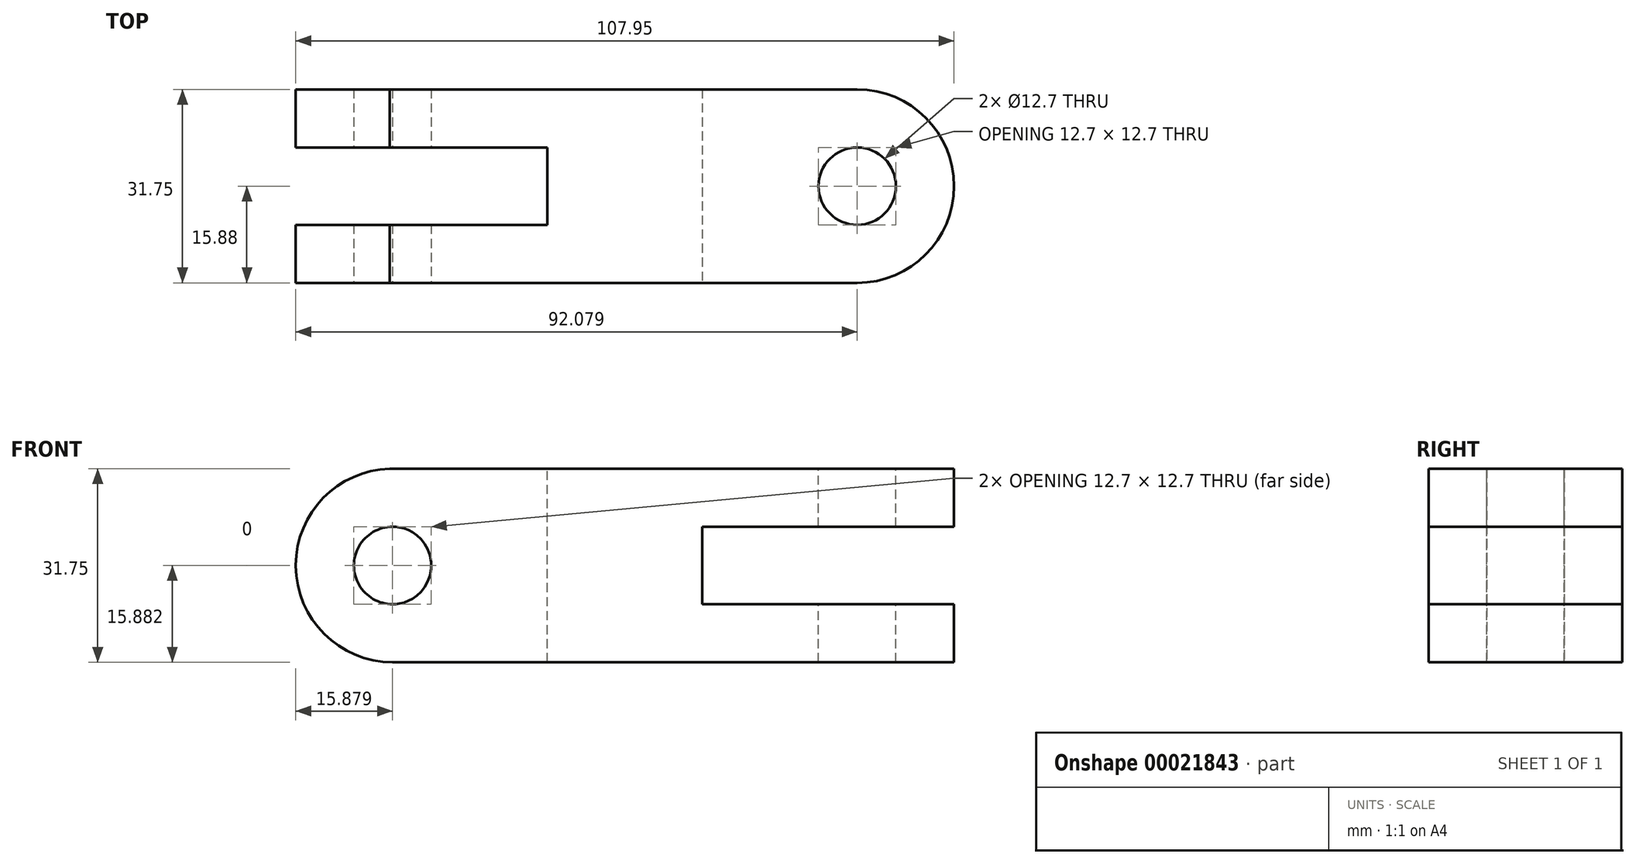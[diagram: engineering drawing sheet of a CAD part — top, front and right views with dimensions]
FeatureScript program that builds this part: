
annotation { "Feature Type Name" : "Feature", "Feature Type Description" : "" }
export const myFeature = defineFeature(function(context is Context, id is Id, definition is map)
    precondition{}
    {
        {
            var Q0;
            Q0=qCreatedBy(makeId("Top.planeOp"),FACE);
            var sketch = newSketch(context, id + "F0", { "sketchPlane" : qUnion([Q0])});
            skLineSegment(sketch, "E0.bottom", {"start": v(-44.49, 22.47) * mm, "end": v(63.46, 22.47) * mm});
            skLineSegment(sketch, "E0.top", {"start": v(-44.49, -9.28) * mm, "end": v(63.46, -9.28) * mm});
            skLineSegment(sketch, "E0.left", {"start": v(-44.49, 22.47) * mm, "end": v(-44.49, -9.28) * mm});
            skLineSegment(sketch, "E0.right", {"start": v(63.46, 22.47) * mm, "end": v(63.46, -9.28) * mm});
            skSolve(sketch);
        }
        {
            var Q0;
            Q0=makeQuery(id+"F0.imprint","IMPRINT",FACE,{"disambiguationData":[TD([[makeQuery(id+"F0.imprint","IMPRINT",EDGE,{"derivedFrom":sQuery(id+"F0.wireOp",EDGE,"E0.bottom")}),-1.0]])]});
            extrude(context, id + "F1", {"entities" : qUnion([Q0]), "depth" : 31.75 * mm});
        }
        {
            var Q0;
            Q0=makeQuery(id+"F1.opExtrude","CAP_FACE",FACE,{"disambiguationData":[OSD([sQuery(id+"F0.wireOp",EDGE,"E0.bottom"),sQuery(id+"F0.wireOp",EDGE,"E0.top"),sQuery(id+"F0.wireOp",EDGE,"E0.left"),sQuery(id+"F0.wireOp",EDGE,"E0.right")])],"isStart":false});
            var sketch = newSketch(context, id + "F2", { "sketchPlane" : qUnion([Q0])});
            skLineSegment(sketch, "E1.0", {"start": v(-44.49, 12.95) * mm, "end": v(-3.21, 12.95) * mm});
            skLineSegment(sketch, "E2.0", {"start": v(-44.49, 0.25) * mm, "end": v(-3.21, 0.25) * mm});
            skLineSegment(sketch, "E3.0", {"start": v(-3.21, 12.95) * mm, "end": v(-3.21, 0.25) * mm});
            skLineSegment(sketch, "E4.0", {"start": v(47.59, 22.47) * mm, "end": v(47.59, -9.28) * mm, "construction": true});
            skArc(sketch, "E5", {"start": v(47.59, -9.28) * mm, "mid": v(63.46, 6.6) * mm, "end": v(47.59, 22.47) * mm});
            skCircle(sketch, "E6", {"center": v(47.59, 6.6) * mm, "radius": 6.35 * mm});
            skSolve(sketch);
        }
        {
            var Q0;
            Q0=makeQuery(id+"F1.opExtrude","SWEPT_FACE",FACE,{"disambiguationData":[OSD([sQuery(id+"F0.wireOp",EDGE,"E0.top")])]});
            var sketch = newSketch(context, id + "F3", { "sketchPlane" : qUnion([Q0])});
            skLineSegment(sketch, "E7.0", {"start": v(22.19, 22.23) * mm, "end": v(63.46, 22.23) * mm});
            skLineSegment(sketch, "E8.0", {"start": v(22.19, 9.53) * mm, "end": v(63.46, 9.53) * mm});
            skLineSegment(sketch, "E9.0", {"start": v(-28.61, 31.84) * mm, "end": v(-28.61, 31.76) * mm, "construction": true});
            skLineSegment(sketch, "E10.0", {"start": v(22.19, 22.23) * mm, "end": v(22.19, 9.53) * mm});
            skLineSegment(sketch, "E11.right", {"start": v(63.46, 22.23) * mm, "end": v(63.46, 9.53) * mm});
            skLineSegment(sketch, "E12.bottom", {"start": v(41.87, 36.55) * mm, "end": v(40.98, 36.55) * mm});
            skLineSegment(sketch, "E12.top", {"start": v(41.87, 36.55) * mm, "end": v(40.98, 36.55) * mm});
            skPoint(sketch, "E13.center.orphan", {"position": v(-28.61, 15.88) * mm});
            skPoint(sketch, "E14.trimOffspring.end.orphan", {"position": v(-28.61, 0) * mm});
            skLineSegment(sketch, "E15.0", {"start": v(-28.61, 31.75) * mm, "end": v(-28.61, 0) * mm});
            skCircle(sketch, "E16", {"center": v(-28.61, 15.88) * mm, "radius": 6.35 * mm});
            skArc(sketch, "E17", {"start": v(-28.16, 31.75) * mm, "mid": v(-44.48, 16.1) * mm, "end": v(-28.61, 0) * mm});
            skLineSegment(sketch, "E18.0", {"start": v(63.46, 31.75) * mm, "end": v(63.46, 0) * mm});
            skLineSegment(sketch, "E19", {"start": v(-28.16, 31.75) * mm, "end": v(63.46, 31.75) * mm});
            skLineSegment(sketch, "E20", {"start": v(-28.61, 0) * mm, "end": v(63.46, 0) * mm});
            skSolve(sketch);
        }
        {
            var Q0;
            {var subQ2=sQuery(id+"F2.wireOp",EDGE,"E1.0");Q0=makeQuery(id+"F2.imprint","IMPRINT",FACE,{"disambiguationData":[TD([[makeQuery(id+"F2.imprint","IMPRINT",EDGE,{"derivedFrom":subQ2}),-1.0]])]});}
            var Q1;
            Q1=makeQuery(id+"F2.imprint","IMPRINT",FACE,{"disambiguationData":[TD([[makeQuery(id+"F2.imprint","IMPRINT",EDGE,{"derivedFrom":sQuery(id+"F2.wireOp",EDGE,"E6")}),1.0]])]});
            var Q2;
            {var subQ1=sQuery(id+"F2.wireOp",EDGE,"E5");var subQ3=makeQuery(id+"F1.opExtrude","CAP_EDGE",EDGE,{"disambiguationData":[OSD([sQuery(id+"F0.wireOp",EDGE,"E0.bottom")])],"isStart":false});var subQ5=makeQuery(id+"F2.imprint","INTERSECT",VERTEX,{"derivedFrom":[subQ3,subQ1]});Q2=makeQuery(id+"F2.imprint","IMPRINT",FACE,{"disambiguationData":[TD([[makeQuery(id+"F2.imprint","IMPRINT",EDGE,{"disambiguationData":[TD([[subQ5,1.0]])],"derivedFrom":subQ1}),-1.0]])]});}
            var Q3;
            {var subQ1=sQuery(id+"F2.wireOp",EDGE,"E5");var subQ3=makeQuery(id+"F1.opExtrude","CAP_EDGE",EDGE,{"disambiguationData":[OSD([sQuery(id+"F0.wireOp",EDGE,"E0.top")])],"isStart":false});var subQ5=makeQuery(id+"F2.imprint","INTERSECT",VERTEX,{"derivedFrom":[subQ3,subQ1]});Q3=makeQuery(id+"F2.imprint","IMPRINT",FACE,{"disambiguationData":[TD([[makeQuery(id+"F2.imprint","IMPRINT",EDGE,{"disambiguationData":[TD([[subQ5,-1.0]])],"derivedFrom":subQ1}),-1.0]])]});}
            extrude(context, id + "F4", {"entities" : qUnion([Q0, Q1, Q2, Q3]), "operationType" : NewBodyOperationType.REMOVE, "endBound" : BoundingType.THROUGH_ALL, "oppositeDirection" : true, "depth" : 25.4 * mm});
        }
        {
            var Q0;
            {var subQ1=sQuery(id+"F2.wireOp",EDGE,"E5");var subQ3=makeQuery(id+"F1.opExtrude","CAP_EDGE",EDGE,{"disambiguationData":[OSD([sQuery(id+"F0.wireOp",EDGE,"E0.bottom")])],"isStart":false});var subQ5=makeQuery(id+"F2.imprint","INTERSECT",VERTEX,{"derivedFrom":[subQ3,subQ1]});Q0=makeQuery(id+"F2.imprint","IMPRINT",FACE,{"disambiguationData":[TD([[makeQuery(id+"F2.imprint","IMPRINT",EDGE,{"disambiguationData":[TD([[subQ5,1.0]])],"derivedFrom":subQ1}),-1.0]])]});}
            var Q1;
            {var subQ1=sQuery(id+"F2.wireOp",EDGE,"E5");var subQ3=makeQuery(id+"F1.opExtrude","CAP_EDGE",EDGE,{"disambiguationData":[OSD([sQuery(id+"F0.wireOp",EDGE,"E0.top")])],"isStart":false});var subQ5=makeQuery(id+"F2.imprint","INTERSECT",VERTEX,{"derivedFrom":[subQ3,subQ1]});Q1=makeQuery(id+"F2.imprint","IMPRINT",FACE,{"disambiguationData":[TD([[makeQuery(id+"F2.imprint","IMPRINT",EDGE,{"disambiguationData":[TD([[subQ5,-1.0]])],"derivedFrom":subQ1}),-1.0]])]});}
            var Q2;
            Q2=makeQuery(id+"F2.imprint","IMPRINT",FACE,{"disambiguationData":[TD([[makeQuery(id+"F2.imprint","IMPRINT",EDGE,{"derivedFrom":sQuery(id+"F2.wireOp",EDGE,"E6")}),1.0]])]});
            var Q3;
            {var subQ2=sQuery(id+"F2.wireOp",EDGE,"E1.0");Q3=makeQuery(id+"F2.imprint","IMPRINT",FACE,{"disambiguationData":[TD([[makeQuery(id+"F2.imprint","IMPRINT",EDGE,{"derivedFrom":subQ2}),-1.0]])]});}
            extrude(context, id + "F5", {"entities" : qUnion([Q0, Q1, Q2, Q3]), "operationType" : NewBodyOperationType.REMOVE, "oppositeDirection" : true, "depth" : 25.4 * mm});
        }
        {
            var Q0;
            {var subQ0=sQuery(id+"F0.wireOp",EDGE,"E0.top");var subQ1=makeQuery(id+"F1.opExtrude","CAP_EDGE",EDGE,{"disambiguationData":[OSD([subQ0])],"isStart":false});var subQ2=sQuery(id+"F3.wireOp",EDGE,"E17");var subQ3=makeQuery(id+"F3.imprint","INTERSECT",VERTEX,{"derivedFrom":[subQ1,subQ2]});Q0=makeQuery(id+"F3.imprint","IMPRINT",FACE,{"disambiguationData":[TD([[makeQuery(id+"F3.imprint","IMPRINT",EDGE,{"disambiguationData":[TD([[subQ3,-1.0]])],"derivedFrom":subQ2}),-1.0]])]});}
            var Q1;
            {var subQ2=sQuery(id+"F3.wireOp",EDGE,"E17");var subQ6=sQuery(id+"F3.wireOp",EDGE,"E15.0");var subQ8=makeQuery(id+"F3.imprint","INTERSECT",VERTEX,{"derivedFrom":[subQ6,subQ2]});Q1=makeQuery(id+"F3.imprint","IMPRINT",FACE,{"disambiguationData":[TD([[makeQuery(id+"F3.imprint","IMPRINT",EDGE,{"disambiguationData":[TD([[subQ8,-1.0]])],"derivedFrom":subQ6}),-1.0]])]});}
            var Q2;
            {var subQ0=sQuery(id+"F3.wireOp",EDGE,"E16");var subQ1=sQuery(id+"F3.wireOp",EDGE,"E15.0");var subQ3=makeQuery(id+"F3.imprint","INTERSECT",VERTEX,{"disambiguationData":[OD(0.0)],"derivedFrom":[subQ1,subQ0]});Q2=makeQuery(id+"F3.imprint","IMPRINT",FACE,{"disambiguationData":[TD([[makeQuery(id+"F3.imprint","IMPRINT",EDGE,{"disambiguationData":[TD([[subQ3,-1.0]])],"derivedFrom":subQ1}),-1.0]])]});}
            var Q3;
            {var subQ0=sQuery(id+"F3.wireOp",EDGE,"E16");var subQ1=sQuery(id+"F3.wireOp",EDGE,"E15.0");var subQ3=makeQuery(id+"F3.imprint","INTERSECT",VERTEX,{"disambiguationData":[OD(0.0)],"derivedFrom":[subQ1,subQ0]});Q3=makeQuery(id+"F3.imprint","IMPRINT",FACE,{"disambiguationData":[TD([[makeQuery(id+"F3.imprint","IMPRINT",EDGE,{"disambiguationData":[TD([[subQ3,-1.0]])],"derivedFrom":subQ1}),1.0]])]});}
            var Q4;
            {var subQ2=sQuery(id+"F3.wireOp",EDGE,"E7.0");Q4=makeQuery(id+"F3.imprint","IMPRINT",FACE,{"disambiguationData":[TD([[makeQuery(id+"F3.imprint","IMPRINT",EDGE,{"derivedFrom":subQ2}),-1.0]])]});}
            extrude(context, id + "F6", {"entities" : qUnion([Q0, Q1, Q2, Q3, Q4]), "operationType" : NewBodyOperationType.REMOVE, "endBound" : BoundingType.THROUGH_ALL, "oppositeDirection" : true, "depth" : 25.4 * mm});
        }
    });
